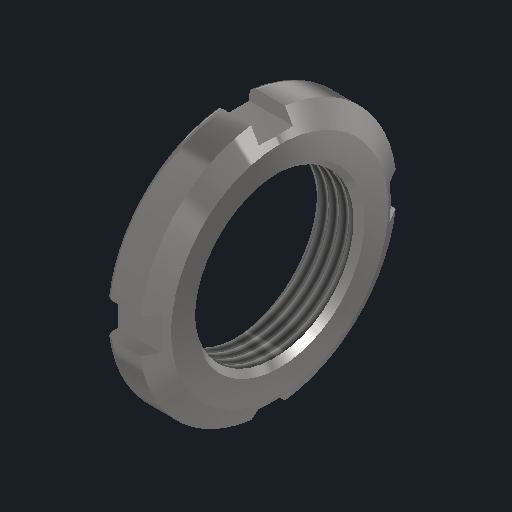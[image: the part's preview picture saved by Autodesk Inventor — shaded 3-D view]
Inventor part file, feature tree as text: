
AUTODESK INVENTOR PART (.ipt)
format: ipt  version: 2022 (Build 260153000, 153)  size: 180,224 bytes
history: native  units: mm (DEFAULTED — no unit token found)
features: other x28, sketch x2, revolve x1, thread x1, extrude x1
ambient origin geometry x8: Origin, YZ Plane, XZ Plane, XY Plane, X Axis, Y Axis, Z Axis, Center Point
bodies: Solid1 (feature_tree)
feature tree (33):
  revolve  "Revolution1"  [1 undecoded]
  thread  "Thread1"  [1 undecoded]
  extrude  "Extrusion1"  [1 undecoded]
  other  "km_XY"
  other  "km_YZ"
  other  "km_ZX"
  other  "km_X"
  other  "km_Y"
  other  "km_Z"
  other  "km_Center"
  other  "km2_XY"
  other  "km2_YZ"
  other  "km2_ZX"
  other  "km2_X"
  other  "km2_Y"
  other  "km2_Z"
  other  "km2_Center"
  other  "ln_XY"
  other  "ln_YZ"
  other  "ln_ZX"
  other  "ln_X"
  other  "ln_Y"
  other  "ln_Z"
  other  "ln_Center"
  other  "nut_XY"
  other  "nut_YZ"
  other  "nut_ZX"
  other  "nut_X"
  other  "nut_Y"
  other  "nut_Z"
  other  "nut_Center"
  sketch  "Sketch_3"  dims[d0=360.0deg d1=5.376mm d2=0.0mm d3=14.0mm d4=0.0mm]
  sketch  "Sketch_6"  dims[d5=0.0mm d6=0.0mm d7=0.0mm]
note: 3 required parameter values undecoded (feature->parameter linkage not recoverable at this tier; creation-order binding heuristic only, values carry confidence <= 0.55)